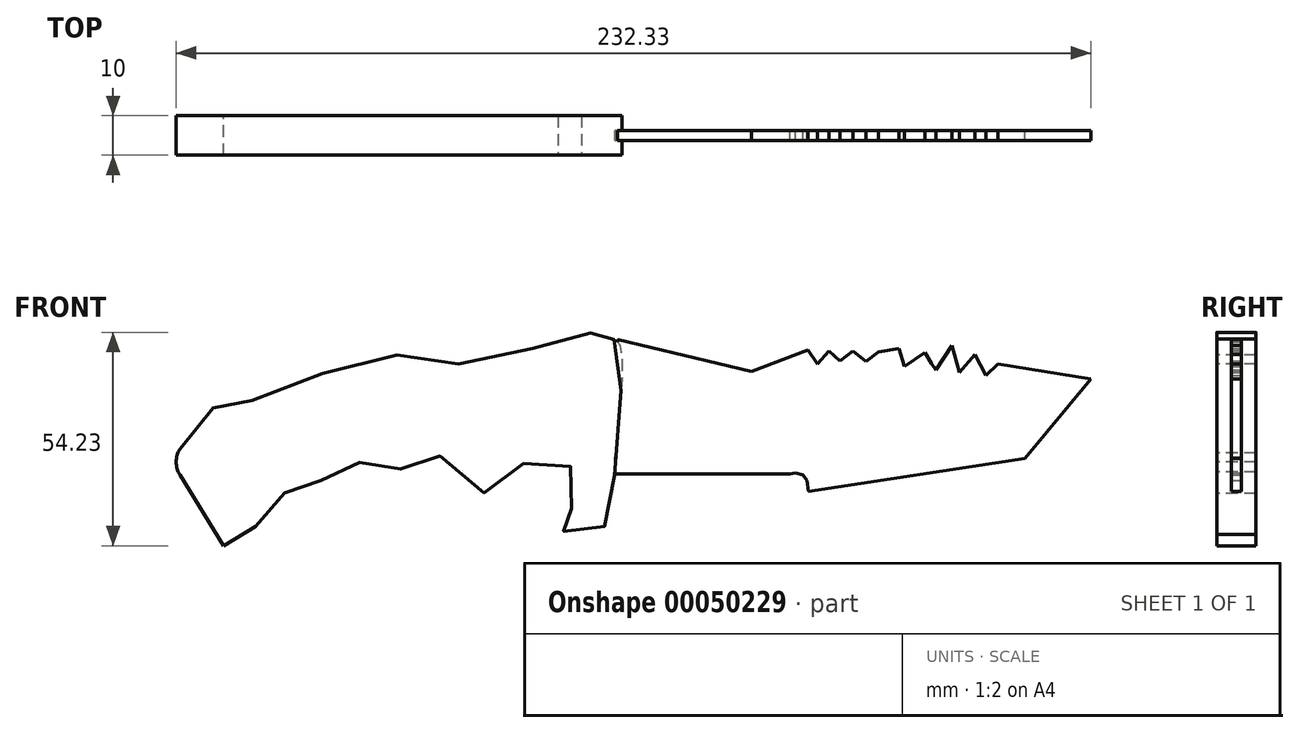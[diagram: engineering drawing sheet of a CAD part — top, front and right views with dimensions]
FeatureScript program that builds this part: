
annotation { "Feature Type Name" : "Feature", "Feature Type Description" : "" }
export const myFeature = defineFeature(function(context is Context, id is Id, definition is map)
    precondition{}
    {
        {
            var Q0;
            Q0=qCreatedBy(makeId("Front.planeOp"),FACE);
            var sketch = newSketch(context, id + "F0", { "sketchPlane" : qUnion([Q0])});
            skLineSegment(sketch, "E0", {"start": v(-136.95, -5.52) * mm, "end": v(-125.85, -23.44) * mm});
            skFitSpline(sketch, "E1", {"points": [v(-139, -2.2) * mm, v(-128.16, 11.79) * mm, v(-119, 13.31) * mm, v(-85.22, 24.86) * mm, v(-61.25, 22.9) * mm, v(-33.13, 30.75) * mm, v(-29.86, 29) * mm, v(-25.94, 28.57) * mm, v(-26.38, -2.2) * mm, v(-29.86, -19.16) * mm, v(-39.89, -19.6) * mm, v(-40.54, -17.2) * mm, v(-34.88, -9.14) * mm, v(-45.56, 0) * mm, v(-58.42, -10.23) * mm, v(-72.58, 0) * mm, v(-82.6, -4.56) * mm, v(-93.07, -2.2) * mm, v(-103.1, -8.05) * mm, v(-110.94, -10.44) * mm, v(-119, -19.6) * mm, v(-125.85, -23.44) * mm, v(-119.88, -36.82) * mm], "startDerivative": vector(209.6, 344.62) * mm, "endDerivative": vector(223.66, -342.56) * mm});
            skArc(sketch, "E2.filletArc", {"start": v(-136.94, 1.18) * mm, "mid": v(-137.9, -2.17) * mm, "end": v(-136.95, -5.52) * mm});
            skSolve(sketch);
        }
        {
            var Q0;
            Q0=makeQuery(id+"F0.imprint","IMPRINT",FACE,{"disambiguationData":[TD([[makeQuery(id+"F0.imprint","IMPRINT",EDGE,{"derivedFrom":sQuery(id+"F0.wireOp",EDGE,"E0")}),1.0]])]});
            extrude(context, id + "F1", {"entities" : qUnion([Q0]), "depth" : 10 * mm});
        }
        {
            var Q0;
            Q0=makeQuery(id+"F0.imprint","IMPRINT",FACE,{"disambiguationData":[TD([[makeQuery(id+"F0.imprint","IMPRINT",EDGE,{"derivedFrom":sQuery(id+"F0.wireOp",EDGE,"E0")}),1.0]])]});
            extrude(context, id + "F2", {"entities" : qUnion([Q0]), "operationType" : NewBodyOperationType.ADD, "depth" : 10 * mm});
        }
        {
            var Q0;
            Q0=qCreatedBy(makeId("Front.planeOp"),FACE);
            cPlane(context, id + "F3", {"entities" : qUnion([Q0]), "cplaneType" : CPlaneType.OFFSET, "offset" : 5 * mm, "width" : 150 * mm, "height" : 150 * mm});
        }
        {
            var Q0;
            Q0=qCreatedBy(id+"F3.planeOp",FACE);
            var sketch = newSketch(context, id + "F4", { "sketchPlane" : qUnion([Q0])});
            skLineSegment(sketch, "E3", {"start": v(-25.75, 28.94) * mm, "end": v(8.2, 20.82) * mm});
            skLineSegment(sketch, "E4", {"start": v(8.2, 20.82) * mm, "end": v(22.57, 26.23) * mm});
            skLineSegment(sketch, "E5", {"start": v(22.57, 26.23) * mm, "end": v(25.07, 22.7) * mm});
            skLineSegment(sketch, "E6", {"start": v(25.07, 22.7) * mm, "end": v(27.99, 26.03) * mm});
            skLineSegment(sketch, "E7", {"start": v(27.99, 26.03) * mm, "end": v(30.7, 23.53) * mm});
            skLineSegment(sketch, "E8", {"start": v(30.7, 23.53) * mm, "end": v(34.03, 26.03) * mm});
            skLineSegment(sketch, "E9", {"start": v(34.03, 26.03) * mm, "end": v(37.36, 23.32) * mm});
            skLineSegment(sketch, "E10", {"start": v(37.36, 23.32) * mm, "end": v(40.48, 25.82) * mm});
            skLineSegment(sketch, "E11", {"start": v(40.48, 25.82) * mm, "end": v(45.7, 26.65) * mm});
            skLineSegment(sketch, "E12", {"start": v(45.7, 26.65) * mm, "end": v(47.15, 22.07) * mm});
            skLineSegment(sketch, "E13", {"start": v(47.15, 22.07) * mm, "end": v(52.36, 25.6) * mm});
            skLineSegment(sketch, "E14", {"start": v(52.36, 25.6) * mm, "end": v(54.02, 22.9) * mm});
            skLineSegment(sketch, "E15", {"start": v(54.02, 22.9) * mm, "end": v(55.06, 21.24) * mm});
            skLineSegment(sketch, "E16", {"start": v(55.06, 21.24) * mm, "end": v(59.23, 27.48) * mm});
            skLineSegment(sketch, "E17", {"start": v(59.23, 27.48) * mm, "end": v(61.1, 20.61) * mm});
            skLineSegment(sketch, "E18", {"start": v(61.1, 20.61) * mm, "end": v(65.06, 25.2) * mm});
            skLineSegment(sketch, "E19", {"start": v(65.06, 25.2) * mm, "end": v(67.77, 19.78) * mm});
            skLineSegment(sketch, "E20", {"start": v(67.77, 19.78) * mm, "end": v(70.9, 22.7) * mm});
            skLineSegment(sketch, "E21", {"start": v(70.9, 22.7) * mm, "end": v(94.43, 18.94) * mm});
            skLineSegment(sketch, "E22", {"start": v(94.43, 18.94) * mm, "end": v(77.77, -1.26) * mm});
            skLineSegment(sketch, "E23", {"start": v(77.77, -1.26) * mm, "end": v(22.78, -9.59) * mm});
            skLineSegment(sketch, "E24", {"start": v(22.78, -9.59) * mm, "end": v(22.37, -6.85) * mm});
            skLineSegment(sketch, "E25", {"start": v(22.37, -6.85) * mm, "end": v(21.32, -5.42) * mm});
            skLineSegment(sketch, "E26", {"start": v(21.32, -5.42) * mm, "end": v(19.45, -5) * mm});
            skLineSegment(sketch, "E27", {"start": v(19.45, -5) * mm, "end": v(18, -5.22) * mm});
            skLineSegment(sketch, "E28", {"start": v(18, -5.22) * mm, "end": v(-26.37, -5.22) * mm});
            skLineSegment(sketch, "E29", {"start": v(-26.37, -5.22) * mm, "end": v(-25.75, 28.94) * mm});
            skSolve(sketch);
        }
        {
            var Q0;
            Q0=makeQuery(id+"F4.imprint","IMPRINT",FACE,{"disambiguationData":[TD([[makeQuery(id+"F4.imprint","IMPRINT",EDGE,{"derivedFrom":sQuery(id+"F4.wireOp",EDGE,"E3")}),-1.0]])]});
            extrude(context, id + "F5", {"entities" : qUnion([Q0]), "operationType" : NewBodyOperationType.ADD, "endBound" : BoundingType.SYMMETRIC, "depth" : 2.5 * mm});
        }
    });
